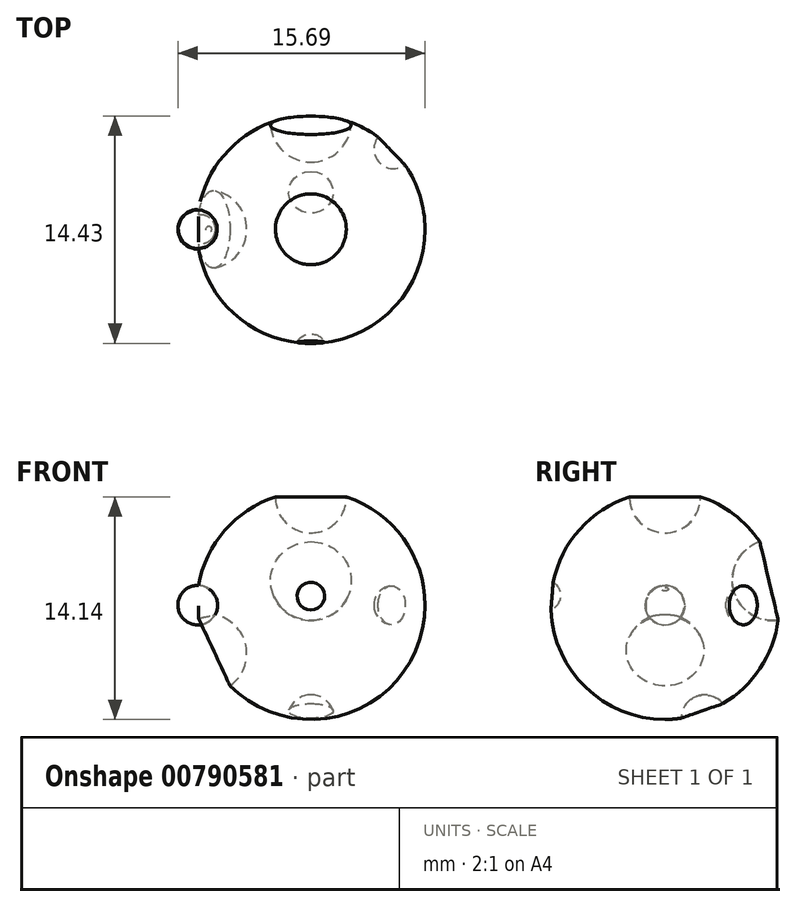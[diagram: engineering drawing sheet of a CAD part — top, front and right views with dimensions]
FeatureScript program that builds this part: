
annotation { "Feature Type Name" : "Feature", "Feature Type Description" : "" }
export const myFeature = defineFeature(function(context is Context, id is Id, definition is map)
    precondition{}
    {
        {
            var Q0;
            Q0=qCreatedBy(makeId("Front.planeOp"),FACE);
            var sketch = newSketch(context, id + "F0", { "sketchPlane" : qUnion([Q0])});
            skArc(sketch, "E0", {"start": v(7.25, 0) * mm, "mid": v(0, 7.25) * mm, "end": v(-7.25, 0) * mm});
            skLineSegment(sketch, "E1", {"start": v(0, 0) * mm, "end": v(7.25, 0) * mm});
            skLineSegment(sketch, "E2", {"start": v(0, 0) * mm, "end": v(-7.25, 0) * mm});
            skSolve(sketch);
        }
        {
            var Q0;
            Q0=makeQuery(id+"F0.imprint","IMPRINT",FACE,{"disambiguationData":[TD([[makeQuery(id+"F0.imprint","IMPRINT",EDGE,{"derivedFrom":sQuery(id+"F0.wireOp",EDGE,"E0")}),1.0]])]});
            var Q1;
            Q1=sQuery(id+"F0.wireOp",EDGE,"E1");
            revolve(context, id + "F1", {"surfaceOperationType" : NewSurfaceOperationType.NEW, "entities" : qUnion([Q0]), "axis" : qUnion([Q1]), "revolveType" : RevolveType.FULL});
        }
        {
            var Q0;
            Q0=qCreatedBy(makeId("Right.planeOp"),FACE);
            var sketch = newSketch(context, id + "F2", { "sketchPlane" : qUnion([Q0])});
            skArc(sketch, "E3", {"start": v(3.4, -8.42) * mm, "mid": v(3.74, -6.32) * mm, "end": v(1.65, -5.97) * mm});
            skLineSegment(sketch, "E4", {"start": v(2.52, -7.2) * mm, "end": v(3.4, -8.42) * mm});
            skLineSegment(sketch, "E5", {"start": v(2.52, -7.2) * mm, "end": v(1.65, -5.97) * mm});
            skSolve(sketch);
        }
        {
            var Q0;
            Q0 = qSketchRegion(id + "F2", true);
            var Q1;
            Q1=sQuery(id+"F2.wireOp",EDGE,"E4");
            revolve(context, id + "F3", {"operationType" : NewBodyOperationType.REMOVE, "surfaceOperationType" : NewSurfaceOperationType.NEW, "entities" : qUnion([Q0]), "axis" : qUnion([Q1]), "revolveType" : RevolveType.FULL, "oppositeDirection" : true});
        }
        {
            var Q0;
            Q0=qCreatedBy(makeId("Front.planeOp"),FACE);
            var sketch = newSketch(context, id + "F4", { "sketchPlane" : qUnion([Q0])});
            skArc(sketch, "E6", {"start": v(-6.57, -0.57) * mm, "mid": v(-9.07, -3.07) * mm, "end": v(-6.57, -5.57) * mm});
            skLineSegment(sketch, "E7", {"start": v(-6.57, -3.07) * mm, "end": v(-6.57, -5.57) * mm});
            skLineSegment(sketch, "E8", {"start": v(-6.57, -5.57) * mm, "end": v(-6.57, -0.57) * mm});
            skSolve(sketch);
        }
        {
            var Q0;
            {var subQ0=sQuery(id+"F4.wireOp",EDGE,"E6");Q0=makeQuery(id+"F4.imprint","IMPRINT",FACE,{"disambiguationData":[TD([[makeQuery(id+"F4.imprint","IMPRINT",EDGE,{"derivedFrom":subQ0}),1.0]])]});}
            var Q1;
            Q1=sQuery(id+"F4.wireOp",EDGE,"E8");
            revolve(context, id + "F5", {"operationType" : NewBodyOperationType.REMOVE, "surfaceOperationType" : NewSurfaceOperationType.NEW, "entities" : qUnion([Q0]), "axis" : qUnion([Q1]), "revolveType" : RevolveType.FULL, "oppositeDirection" : true});
        }
        {
            var Q0;
            Q0=qCreatedBy(makeId("Right.planeOp"),FACE);
            var sketch = newSketch(context, id + "F6", { "sketchPlane" : qUnion([Q0])});
            skArc(sketch, "E9", {"start": v(-7.35, 1.58) * mm, "mid": v(-8.58, 0.9) * mm, "end": v(-7.91, -0.34) * mm});
            skLineSegment(sketch, "E10", {"start": v(-7.91, -0.34) * mm, "end": v(-7.35, 1.58) * mm});
            skSolve(sketch);
        }
        {
            var Q0;
            Q0=makeQuery(id+"F6.imprint","IMPRINT",FACE,{"disambiguationData":[TD([[makeQuery(id+"F6.imprint","IMPRINT",EDGE,{"derivedFrom":sQuery(id+"F6.wireOp",EDGE,"E9")}),1.0]])]});
            var Q1;
            Q1=sQuery(id+"F6.wireOp",EDGE,"E10");
            revolve(context, id + "F7", {"operationType" : NewBodyOperationType.REMOVE, "surfaceOperationType" : NewSurfaceOperationType.NEW, "entities" : qUnion([Q0]), "axis" : qUnion([Q1]), "revolveType" : RevolveType.FULL, "oppositeDirection" : true});
        }
        {
            var Q0;
            Q0=qCreatedBy(makeId("Front.planeOp"),FACE);
            var sketch = newSketch(context, id + "F8", { "sketchPlane" : qUnion([Q0])});
            skArc(sketch, "E11", {"start": v(-7.9, -1.02) * mm, "mid": v(-6.15, -0.7) * mm, "end": v(-6.48, 1.04) * mm});
            skLineSegment(sketch, "E12", {"start": v(-7.9, -1.02) * mm, "end": v(-6.48, 1.04) * mm});
            skSolve(sketch);
        }
        {
            var Q0;
            Q0 = qSketchRegion(id + "F8", true);
            var Q1;
            Q1=sQuery(id+"F8.wireOp",EDGE,"E12");
            var Q2;
            Q2=sQuery(id+"F8.wireOp",EDGE,"E12");
            revolve(context, id + "F9", {"operationType" : NewBodyOperationType.REMOVE, "surfaceOperationType" : NewSurfaceOperationType.ADD, "entities" : qUnion([Q0]), "surfaceEntities" : qUnion([Q1]), "axis" : qUnion([Q2]), "revolveType" : RevolveType.FULL, "oppositeDirection" : true});
        }
        {
            var Q0;
            Q0=qCreatedBy(makeId("Right.planeOp"),FACE);
            var sketch = newSketch(context, id + "F10", { "sketchPlane" : qUnion([Q0])});
            skArc(sketch, "E13", {"start": v(2.24, 6.67) * mm, "mid": v(0.18, 9.1) * mm, "end": v(-2.24, 7.02) * mm});
            skLineSegment(sketch, "E14", {"start": v(0, 6.85) * mm, "end": v(-2.24, 7.02) * mm});
            skLineSegment(sketch, "E15", {"start": v(-2.24, 7.02) * mm, "end": v(2.24, 6.67) * mm});
            skSolve(sketch);
        }
        {
            var Q0;
            Q0 = qSketchRegion(id + "F10", true);
            var Q1;
            Q1=sQuery(id+"F10.wireOp",EDGE,"E15");
            revolve(context, id + "F11", {"operationType" : NewBodyOperationType.REMOVE, "surfaceOperationType" : NewSurfaceOperationType.NEW, "entities" : qUnion([Q0]), "axis" : qUnion([Q1]), "revolveType" : RevolveType.FULL, "oppositeDirection" : true});
        }
        {
            var Q0;
            Q0=qCreatedBy(makeId("Top.planeOp"),FACE);
            var sketch = newSketch(context, id + "F12", { "sketchPlane" : qUnion([Q0])});
            skArc(sketch, "E16", {"start": v(5.93, 4.05) * mm, "mid": v(6.3, 5.78) * mm, "end": v(4.58, 6.15) * mm});
            skLineSegment(sketch, "E17", {"start": v(5.25, 5.1) * mm, "end": v(5.93, 4.05) * mm});
            skLineSegment(sketch, "E18", {"start": v(5.25, 5.1) * mm, "end": v(4.58, 6.15) * mm});
            skSolve(sketch);
        }
        {
            var Q0;
            Q0 = qSketchRegion(id + "F12", true);
            var Q1;
            Q1=sQuery(id+"F12.wireOp",EDGE,"E17");
            revolve(context, id + "F13", {"operationType" : NewBodyOperationType.REMOVE, "surfaceOperationType" : NewSurfaceOperationType.NEW, "entities" : qUnion([Q0]), "axis" : qUnion([Q1]), "revolveType" : RevolveType.FULL, "oppositeDirection" : true});
        }
        {
            var Q0;
            Q0=qCreatedBy(makeId("Right.planeOp"),FACE);
            var sketch = newSketch(context, id + "F14", { "sketchPlane" : qUnion([Q0])});
            skArc(sketch, "E19", {"start": v(7.09, -0.96) * mm, "mid": v(9.4, 1.84) * mm, "end": v(6.6, 4.16) * mm});
            skLineSegment(sketch, "E20", {"start": v(6.84, 1.6) * mm, "end": v(7.09, -0.96) * mm});
            skLineSegment(sketch, "E21", {"start": v(7.09, -0.96) * mm, "end": v(6.84, 1.6) * mm});
            skLineSegment(sketch, "E22", {"start": v(6.84, 1.6) * mm, "end": v(6.6, 4.16) * mm});
            skSolve(sketch);
        }
        {
            var Q0;
            Q0=makeQuery(id+"F14.imprint","IMPRINT",FACE,{"disambiguationData":[TD([[makeQuery(id+"F14.imprint","IMPRINT",EDGE,{"derivedFrom":sQuery(id+"F14.wireOp",EDGE,"E19")}),1.0]])]});
            var Q1;
            Q1=sQuery(id+"F14.wireOp",EDGE,"E22");
            revolve(context, id + "F15", {"operationType" : NewBodyOperationType.REMOVE, "surfaceOperationType" : NewSurfaceOperationType.NEW, "entities" : qUnion([Q0]), "axis" : qUnion([Q1]), "revolveType" : RevolveType.FULL, "oppositeDirection" : true});
        }
    });
